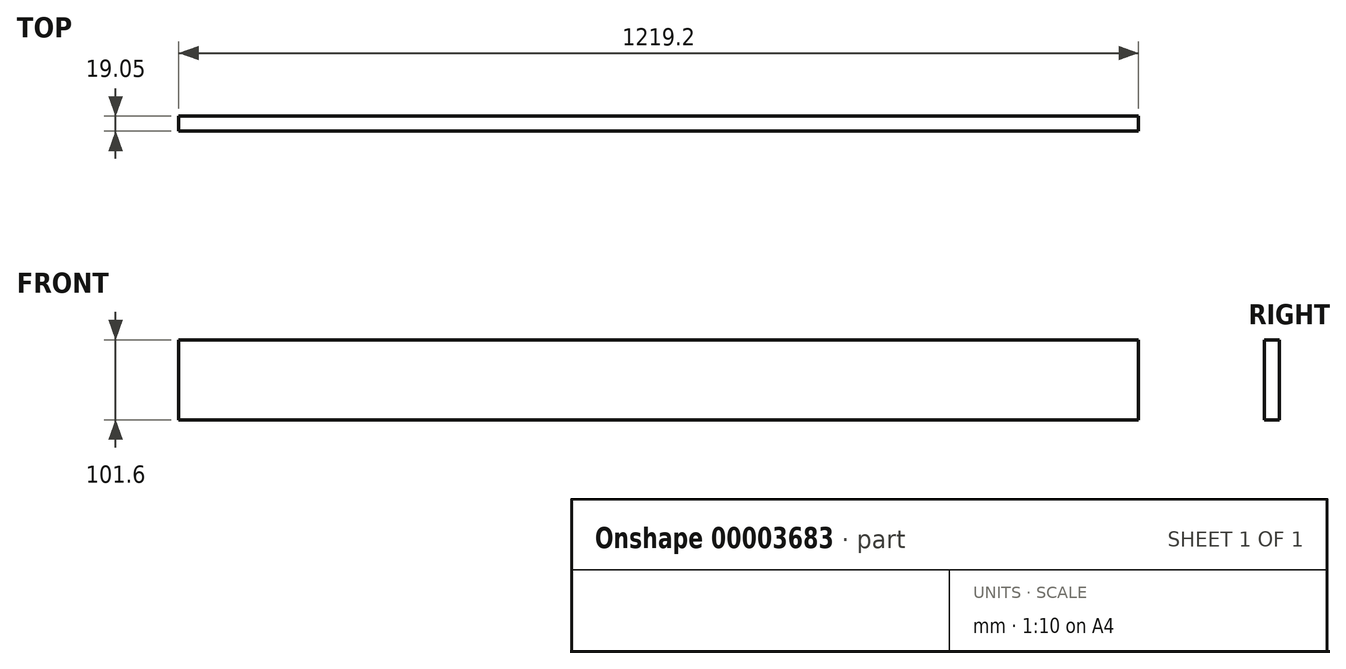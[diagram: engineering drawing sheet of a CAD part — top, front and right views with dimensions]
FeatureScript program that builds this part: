
annotation { "Feature Type Name" : "Feature", "Feature Type Description" : "" }
export const myFeature = defineFeature(function(context is Context, id is Id, definition is map)
    precondition{}
    {
        {
            var Q0;
            Q0=qCreatedBy(makeId("Right.planeOp"),FACE);
            var sketch = newSketch(context, id + "F0", { "sketchPlane" : qUnion([Q0])});
            skLineSegment(sketch, "E0.bottom", {"start": v(0, 0) * mm, "end": v(-19.05, 0) * mm});
            skLineSegment(sketch, "E0.top", {"start": v(0, 101.6) * mm, "end": v(-19.05, 101.6) * mm});
            skLineSegment(sketch, "E0.left", {"start": v(0, 0) * mm, "end": v(0, 101.6) * mm});
            skLineSegment(sketch, "E0.right", {"start": v(-19.05, 0) * mm, "end": v(-19.05, 101.6) * mm});
            skSolve(sketch);
        }
        {
            var Q0;
            Q0=makeQuery(id+"F0.imprint","IMPRINT",FACE,{"disambiguationData":[TD([[makeQuery(id+"F0.imprint","IMPRINT",EDGE,{"derivedFrom":sQuery(id+"F0.wireOp",EDGE,"E0.bottom")}),-1.0]])]});
            extrude(context, id + "F1", {"entities" : qUnion([Q0]), "depth" : 1219.2 * mm});
        }
    });
